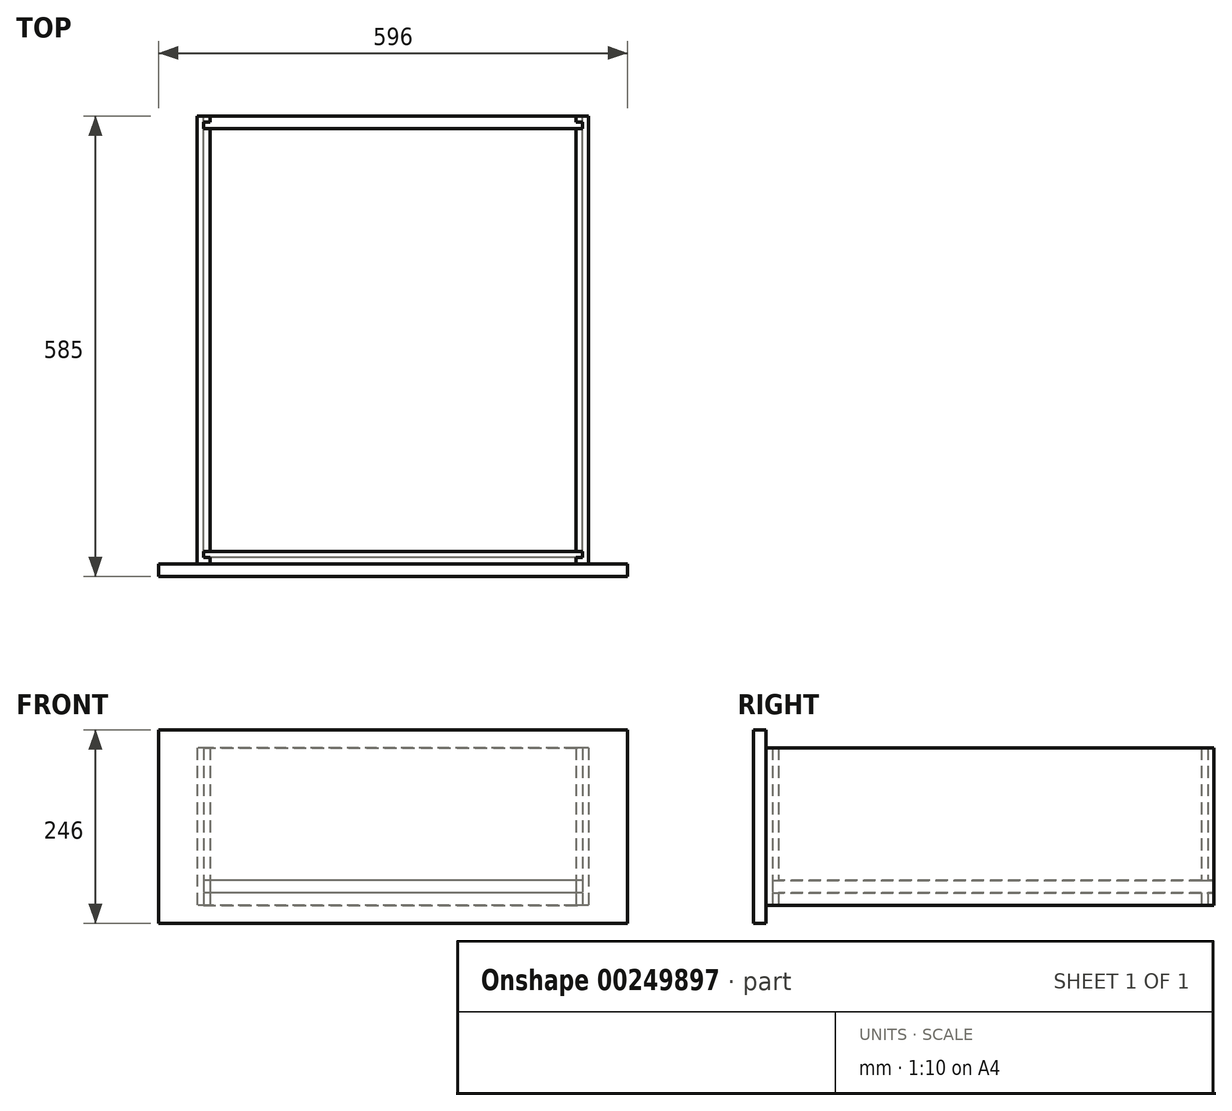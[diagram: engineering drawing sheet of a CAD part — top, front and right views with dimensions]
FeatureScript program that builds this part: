
annotation { "Feature Type Name" : "Feature", "Feature Type Description" : "" }
export const myFeature = defineFeature(function(context is Context, id is Id, definition is map)
    precondition{}
    {
        {
            var Q0;
            Q0=qCreatedBy(makeId("Top.planeOp"),FACE);
            var sketch = newSketch(context, id + "F0", { "sketchPlane" : qUnion([Q0])});
            skLineSegment(sketch, "E0.bottom", {"start": v(248.5, -284.5) * mm, "end": v(-248.5, -284.5) * mm});
            skLineSegment(sketch, "E0.top", {"start": v(248.5, 284.5) * mm, "end": v(-248.5, 284.5) * mm});
            skLineSegment(sketch, "E0.left", {"start": v(248.5, -284.5) * mm, "end": v(248.5, 284.5) * mm});
            skLineSegment(sketch, "E0.right", {"start": v(-248.5, -284.5) * mm, "end": v(-248.5, 284.5) * mm});
            skPoint(sketch, "E0.middle", {"position": v(0, 0) * mm});
            skLineSegment(sketch, "E1.0", {"start": v(232.5, -268.5) * mm, "end": v(-232.5, -268.5) * mm});
            skLineSegment(sketch, "E1.1", {"start": v(-232.5, -268.5) * mm, "end": v(-232.5, 268.5) * mm});
            skLineSegment(sketch, "E1.2", {"start": v(232.5, 268.5) * mm, "end": v(-232.5, 268.5) * mm});
            skLineSegment(sketch, "E2.0", {"start": v(232.5, -268.5) * mm, "end": v(232.5, 268.5) * mm});
            skLineSegment(sketch, "E3", {"start": v(-232.5, 268.5) * mm, "end": v(-240.5, 268.5) * mm});
            skLineSegment(sketch, "E4", {"start": v(-240.5, 268.5) * mm, "end": v(-240.5, 276.5) * mm});
            skLineSegment(sketch, "E5", {"start": v(-240.5, 276.5) * mm, "end": v(-232.5, 276.5) * mm});
            skLineSegment(sketch, "E6", {"start": v(-232.5, 276.5) * mm, "end": v(-232.5, 284.5) * mm});
            skLineSegment(sketch, "E7", {"start": v(232.5, 268.5) * mm, "end": v(240.5, 268.5) * mm});
            skLineSegment(sketch, "E8", {"start": v(240.5, 268.5) * mm, "end": v(240.5, 276.5) * mm});
            skLineSegment(sketch, "E9", {"start": v(240.5, 276.5) * mm, "end": v(232.5, 276.5) * mm});
            skLineSegment(sketch, "E10", {"start": v(232.5, 276.5) * mm, "end": v(232.5, 284.5) * mm});
            skLineSegment(sketch, "E11", {"start": v(232.5, -268.5) * mm, "end": v(240.5, -268.5) * mm});
            skLineSegment(sketch, "E12", {"start": v(240.5, -268.5) * mm, "end": v(240.5, -276.5) * mm});
            skLineSegment(sketch, "E13", {"start": v(240.5, -276.5) * mm, "end": v(232.5, -276.5) * mm});
            skLineSegment(sketch, "E14", {"start": v(232.5, -276.5) * mm, "end": v(232.5, -284.5) * mm});
            skLineSegment(sketch, "E15", {"start": v(-232.5, -268.5) * mm, "end": v(-240.5, -268.5) * mm});
            skLineSegment(sketch, "E16", {"start": v(-240.5, -268.5) * mm, "end": v(-240.5, -276.5) * mm});
            skLineSegment(sketch, "E17", {"start": v(-240.5, -276.5) * mm, "end": v(-232.5, -276.5) * mm});
            skLineSegment(sketch, "E18", {"start": v(-232.5, -276.5) * mm, "end": v(-232.5, -284.5) * mm});
            skSolve(sketch);
        }
        {
            var Q0;
            {var subQ1=sQuery(id+"F0.wireOp",EDGE,"E0.right");Q0=makeQuery(id+"F0.imprint","IMPRINT",FACE,{"disambiguationData":[TD([[makeQuery(id+"F0.imprint","IMPRINT",EDGE,{"derivedFrom":subQ1}),-1.0]])]});}
            extrude(context, id + "F1", {"entities" : qUnion([Q0]), "depth" : 200 * mm});
        }
        {
            var Q0;
            {var subQ1=sQuery(id+"F0.wireOp",EDGE,"E0.left");Q0=makeQuery(id+"F0.imprint","IMPRINT",FACE,{"disambiguationData":[TD([[makeQuery(id+"F0.imprint","IMPRINT",EDGE,{"derivedFrom":subQ1}),1.0]])]});}
            extrude(context, id + "F2", {"entities" : qUnion([Q0]), "depth" : 200 * mm});
        }
        {
            var Q0;
            Q0=makeQuery(id+"F0.imprint","IMPRINT",FACE,{"disambiguationData":[TD([[makeQuery(id+"F0.imprint","IMPRINT",EDGE,{"derivedFrom":sQuery(id+"F0.wireOp",EDGE,"E1.2")}),-1.0]])]});
            extrude(context, id + "F3", {"entities" : qUnion([Q0]), "depth" : 200 * mm});
        }
        {
            var Q0;
            Q0=makeQuery(id+"F0.imprint","IMPRINT",FACE,{"disambiguationData":[TD([[makeQuery(id+"F0.imprint","IMPRINT",EDGE,{"derivedFrom":sQuery(id+"F0.wireOp",EDGE,"E1.0")}),1.0]])]});
            extrude(context, id + "F4", {"entities" : qUnion([Q0]), "depth" : 200 * mm});
        }
        {
            var Q0;
            Q0=makeQuery(id+"F0.imprint","IMPRINT",FACE,{"disambiguationData":[TD([[makeQuery(id+"F0.imprint","IMPRINT",EDGE,{"derivedFrom":sQuery(id+"F0.wireOp",EDGE,"E1.2")}),-1.0]])]});
            extrude(context, id + "F5", {"entities" : qUnion([Q0]), "operationType" : NewBodyOperationType.REMOVE, "depth" : 32 * mm});
        }
        {
            var Q0;
            Q0=makeQuery(id+"F3.opExtrude","SWEPT_FACE",FACE,{"disambiguationData":[OSD([sQuery(id+"F0.wireOp",EDGE,"E0.top")])]});
            var sketch = newSketch(context, id + "F6", { "sketchPlane" : qUnion([Q0])});
            skLineSegment(sketch, "E19.bottom", {"start": v(-240.5, 32) * mm, "end": v(240.5, 32) * mm});
            skLineSegment(sketch, "E19.top", {"start": v(-240.5, 16) * mm, "end": v(240.5, 16) * mm});
            skLineSegment(sketch, "E19.left", {"start": v(-240.5, 32) * mm, "end": v(-240.5, 16) * mm});
            skLineSegment(sketch, "E19.right", {"start": v(240.5, 32) * mm, "end": v(240.5, 16) * mm});
            skSolve(sketch);
        }
        {
            var Q0;
            Q0=makeQuery(id+"F6.imprint","IMPRINT",FACE,{"disambiguationData":[TD([[makeQuery(id+"F6.imprint","IMPRINT",EDGE,{"derivedFrom":sQuery(id+"F6.wireOp",EDGE,"E19.top")}),1.0]])]});
            extrude(context, id + "F7", {"entities" : qUnion([Q0]), "oppositeDirection" : true, "depth" : 561 * mm});
        }
        {
            var Q0;
            Q0=makeQuery(id+"F7.opExtrude","SWEPT_BODY",BODY,{"disambiguationData":[OSD([sQuery(id+"F6.wireOp",EDGE,"E19.bottom"),sQuery(id+"F6.wireOp",EDGE,"E19.top"),sQuery(id+"F6.wireOp",EDGE,"E19.left"),sQuery(id+"F6.wireOp",EDGE,"E19.right")])]});
            var Q1;
            Q1=makeQuery(id+"F2.opExtrude","SWEPT_BODY",BODY,{"disambiguationData":[OSD([sQuery(id+"F0.wireOp",EDGE,"E0.bottom"),sQuery(id+"F0.wireOp",EDGE,"E0.top"),sQuery(id+"F0.wireOp",EDGE,"E0.left"),sQuery(id+"F0.wireOp",EDGE,"E2.0"),sQuery(id+"F0.wireOp",EDGE,"E7"),sQuery(id+"F0.wireOp",EDGE,"E8"),sQuery(id+"F0.wireOp",EDGE,"E9"),sQuery(id+"F0.wireOp",EDGE,"E10"),sQuery(id+"F0.wireOp",EDGE,"E11"),sQuery(id+"F0.wireOp",EDGE,"E12"),sQuery(id+"F0.wireOp",EDGE,"E13"),sQuery(id+"F0.wireOp",EDGE,"E14")])]});
            var Q2;
            Q2=makeQuery(id+"F1.opExtrude","SWEPT_BODY",BODY,{"disambiguationData":[OSD([sQuery(id+"F0.wireOp",EDGE,"E0.bottom"),sQuery(id+"F0.wireOp",EDGE,"E0.top"),sQuery(id+"F0.wireOp",EDGE,"E0.right"),sQuery(id+"F0.wireOp",EDGE,"E1.1"),sQuery(id+"F0.wireOp",EDGE,"E3"),sQuery(id+"F0.wireOp",EDGE,"E4"),sQuery(id+"F0.wireOp",EDGE,"E5"),sQuery(id+"F0.wireOp",EDGE,"E6"),sQuery(id+"F0.wireOp",EDGE,"E15"),sQuery(id+"F0.wireOp",EDGE,"E16"),sQuery(id+"F0.wireOp",EDGE,"E17"),sQuery(id+"F0.wireOp",EDGE,"E18")])]});
            var Q3;
            Q3=makeQuery(id+"F4.opExtrude","SWEPT_BODY",BODY,{"disambiguationData":[OSD([sQuery(id+"F0.wireOp",EDGE,"E0.bottom"),sQuery(id+"F0.wireOp",EDGE,"E1.0"),sQuery(id+"F0.wireOp",EDGE,"E11"),sQuery(id+"F0.wireOp",EDGE,"E12"),sQuery(id+"F0.wireOp",EDGE,"E13"),sQuery(id+"F0.wireOp",EDGE,"E14"),sQuery(id+"F0.wireOp",EDGE,"E15"),sQuery(id+"F0.wireOp",EDGE,"E16"),sQuery(id+"F0.wireOp",EDGE,"E17"),sQuery(id+"F0.wireOp",EDGE,"E18")])]});
            booleanBodies(context, id + "F8", {"operationType" : BooleanOperationType.SUBTRACTION, "tools" : qUnion([Q0]), "targets" : qUnion([Q1, Q2, Q3])});
        }
        {
            var Q0;
            Q0=makeQuery(id+"F6.imprint","IMPRINT",FACE,{"disambiguationData":[TD([[makeQuery(id+"F6.imprint","IMPRINT",EDGE,{"derivedFrom":sQuery(id+"F6.wireOp",EDGE,"E19.top")}),1.0]])]});
            extrude(context, id + "F9", {"entities" : qUnion([Q0]), "oppositeDirection" : true, "depth" : 561 * mm});
        }
        {
            var Q0;
            Q0=makeQuery(id+"F4.opExtrude","SWEPT_FACE",FACE,{"disambiguationData":[OSD([sQuery(id+"F0.wireOp",EDGE,"E0.bottom")])]});
            var sketch = newSketch(context, id + "F10", { "sketchPlane" : qUnion([Q0])});
            skLineSegment(sketch, "E20.bottom", {"start": v(-248.5, 200) * mm, "end": v(248.5, 200) * mm});
            skLineSegment(sketch, "E20.top", {"start": v(-248.5, 0) * mm, "end": v(248.5, 0) * mm});
            skLineSegment(sketch, "E20.left", {"start": v(-248.5, 200) * mm, "end": v(-248.5, 0) * mm});
            skLineSegment(sketch, "E20.right", {"start": v(248.5, 200) * mm, "end": v(248.5, 0) * mm});
            skLineSegment(sketch, "E21.0", {"start": v(-298, 200) * mm, "end": v(-298, 0) * mm, "construction": true});
            skLineSegment(sketch, "E22.0", {"start": v(298, 200) * mm, "end": v(298, 0) * mm, "construction": true});
            skLineSegment(sketch, "E23.0", {"start": v(-248.5, 223) * mm, "end": v(248.5, 223) * mm, "construction": true});
            skLineSegment(sketch, "E24.0", {"start": v(-248.5, -23) * mm, "end": v(248.5, -23) * mm, "construction": true});
            skLineSegment(sketch, "E25.bottom", {"start": v(-298, 223) * mm, "end": v(298, 223) * mm});
            skLineSegment(sketch, "E25.top", {"start": v(-298, -23) * mm, "end": v(298, -23) * mm});
            skLineSegment(sketch, "E25.left", {"start": v(-298, 223) * mm, "end": v(-298, -23) * mm});
            skLineSegment(sketch, "E25.right", {"start": v(298, 223) * mm, "end": v(298, -23) * mm});
            skSolve(sketch);
        }
        {
            var Q0;
            {var subQ1=sQuery(id+"F10.wireOp",EDGE,"E20.left");Q0=makeQuery(id+"F10.imprint","IMPRINT",FACE,{"disambiguationData":[TD([[makeQuery(id+"F10.imprint","IMPRINT",EDGE,{"derivedFrom":subQ1}),-1.0]])]});}
            var Q1;
            {var subQ1=sQuery(id+"F0.wireOp",EDGE,"E0.bottom");var subQ2=makeQuery(id+"F4.opExtrude","SWEPT_EDGE",EDGE,{"disambiguationData":[OSD([subQ1,sQuery(id+"F0.wireOp",EDGE,"E14")])]});Q1=makeQuery(id+"F10.imprint","IMPRINT",FACE,{"disambiguationData":[TD([[makeQuery(id+"F10.imprint","IMPRINT",EDGE,{"derivedFrom":subQ2}),-1.0]])]});}
            var Q2;
            {var subQ2=sQuery(id+"F10.wireOp",EDGE,"E20.left");Q2=makeQuery(id+"F10.imprint","IMPRINT",FACE,{"disambiguationData":[TD([[makeQuery(id+"F10.imprint","IMPRINT",EDGE,{"derivedFrom":subQ2}),1.0]])]});}
            var Q3;
            {var subQ2=sQuery(id+"F10.wireOp",EDGE,"E20.right");Q3=makeQuery(id+"F10.imprint","IMPRINT",FACE,{"disambiguationData":[TD([[makeQuery(id+"F10.imprint","IMPRINT",EDGE,{"derivedFrom":subQ2}),-1.0]])]});}
            extrude(context, id + "F11", {"entities" : qUnion([Q0, Q1, Q2, Q3]), "depth" : 16 * mm});
        }
    });
